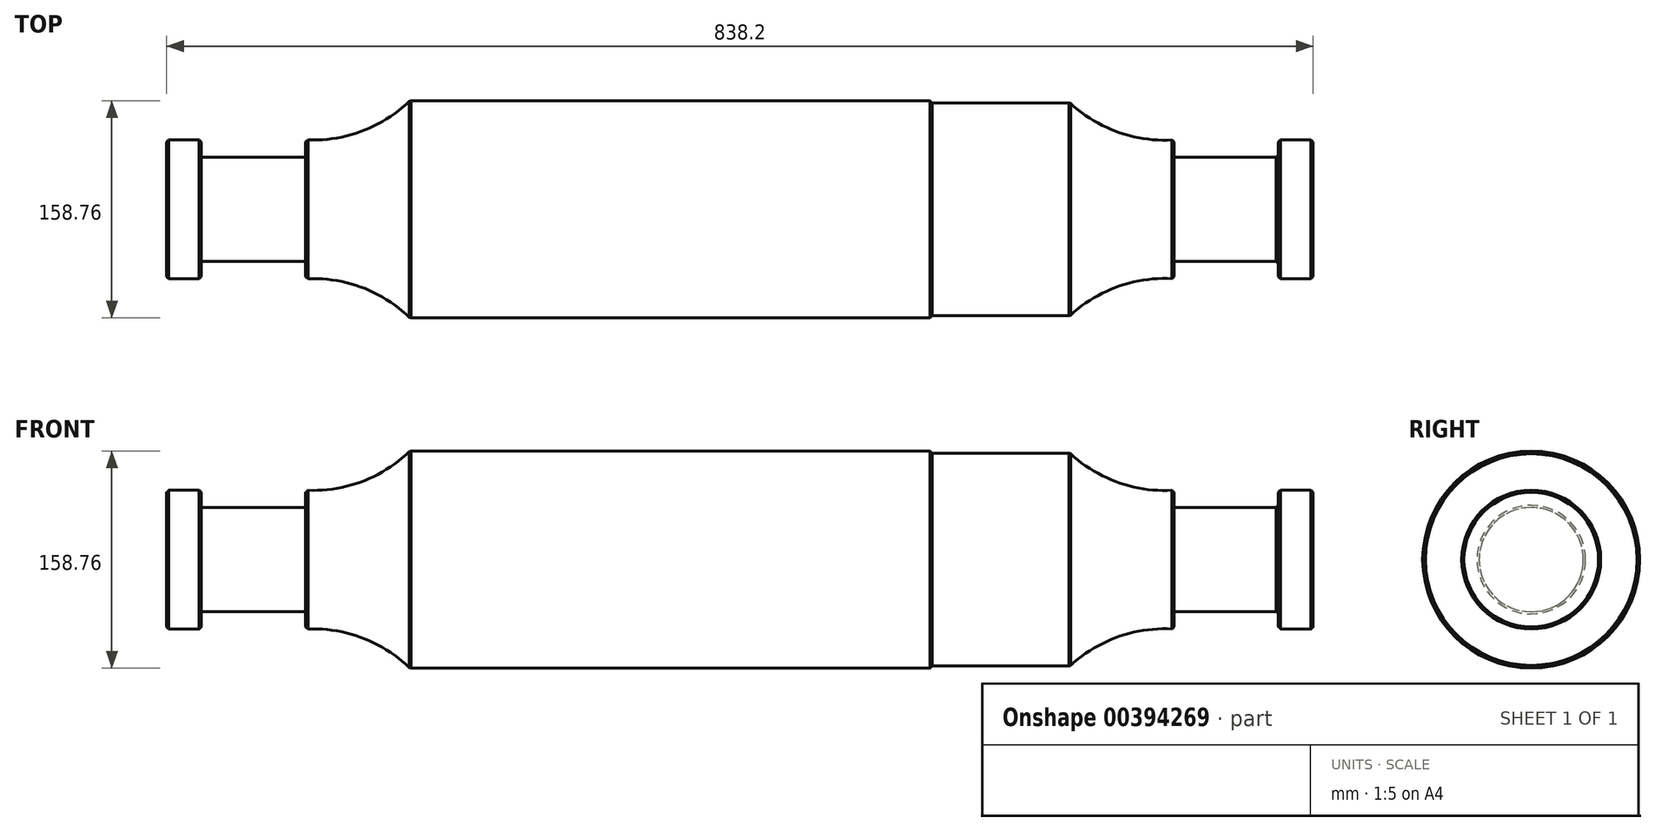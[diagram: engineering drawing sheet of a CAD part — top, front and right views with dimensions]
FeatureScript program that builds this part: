
annotation { "Feature Type Name" : "Feature", "Feature Type Description" : "" }
export const myFeature = defineFeature(function(context is Context, id is Id, definition is map)
    precondition{}
    {
        {
            var Q0;
            Q0=qCreatedBy(makeId("Front.planeOp"),FACE);
            var sketch = newSketch(context, id + "F0", { "sketchPlane" : qUnion([Q0])});
            skLineSegment(sketch, "E0", {"start": v(-447.12, 0) * mm, "end": v(391.08, 0) * mm});
            skLineSegment(sketch, "E1", {"start": v(-447.12, 0) * mm, "end": v(-447.12, 50.8) * mm});
            skLineSegment(sketch, "E2", {"start": v(-447.12, 50.8) * mm, "end": v(-421.72, 50.8) * mm});
            skLineSegment(sketch, "E3", {"start": v(-421.72, 50.8) * mm, "end": v(-421.72, 38.1) * mm});
            skLineSegment(sketch, "E4", {"start": v(-421.72, 38.1) * mm, "end": v(-345.52, 38.1) * mm});
            skLineSegment(sketch, "E5", {"start": v(-345.52, 38.1) * mm, "end": v(-345.52, 50.8) * mm});
            skLineSegment(sketch, "E6", {"start": v(-269.32, 79.37) * mm, "end": v(111.68, 79.38) * mm});
            skLineSegment(sketch, "E7", {"start": v(111.68, 79.38) * mm, "end": v(111.68, 77.79) * mm});
            skLineSegment(sketch, "E8", {"start": v(111.68, 77.79) * mm, "end": v(213.28, 77.79) * mm});
            skLineSegment(sketch, "E9", {"start": v(391.08, 50.8) * mm, "end": v(365.68, 50.8) * mm});
            skLineSegment(sketch, "E10", {"start": v(365.68, 50.8) * mm, "end": v(391.08, 50.8) * mm});
            skLineSegment(sketch, "E11", {"start": v(365.68, 50.8) * mm, "end": v(365.68, 38.1) * mm});
            skLineSegment(sketch, "E12", {"start": v(365.68, 38.1) * mm, "end": v(289.48, 38.1) * mm});
            skLineSegment(sketch, "E13", {"start": v(289.48, 38.1) * mm, "end": v(289.48, 50.8) * mm});
            skArc(sketch, "E14", {"start": v(213.28, 77.79) * mm, "mid": v(248.58, 56.39) * mm, "end": v(289.48, 50.8) * mm});
            skArc(sketch, "E15", {"start": v(-345.52, 50.8) * mm, "mid": v(-304.43, 57.12) * mm, "end": v(-269.32, 79.37) * mm});
            skLineSegment(sketch, "E16", {"start": v(391.08, 50.8) * mm, "end": v(391.08, 0) * mm});
            skSolve(sketch);
        }
        {
            var Q0;
            Q0=makeQuery(id+"F0.imprint","IMPRINT",FACE,{"disambiguationData":[TD([[makeQuery(id+"F0.imprint","IMPRINT",EDGE,{"derivedFrom":sQuery(id+"F0.wireOp",EDGE,"E0")}),1.0]])]});
            var Q1;
            Q1=sQuery(id+"F0.wireOp",EDGE,"E0");
            revolve(context, id + "F1", {"entities" : qUnion([Q0]), "axis" : qUnion([Q1]), "revolveType" : RevolveType.FULL});
        }
        {
            var Q0;
            Q0=makeQuery(id+"F1.opRevolve","SWEPT_EDGE",EDGE,{"disambiguationData":[OSD([sQuery(id+"F0.wireOp",EDGE,"E1"),sQuery(id+"F0.wireOp",EDGE,"E2")])]});
            var Q1;
            Q1=makeQuery(id+"F1.opRevolve","SWEPT_EDGE",EDGE,{"disambiguationData":[OSD([sQuery(id+"F0.wireOp",EDGE,"E2"),sQuery(id+"F0.wireOp",EDGE,"E3")])]});
            var Q2;
            Q2=makeQuery(id+"F1.opRevolve","SWEPT_EDGE",EDGE,{"disambiguationData":[OSD([sQuery(id+"F0.wireOp",EDGE,"E5"),sQuery(id+"F0.wireOp",EDGE,"E15")])]});
            var Q3;
            Q3=makeQuery(id+"F1.opRevolve","SWEPT_EDGE",EDGE,{"disambiguationData":[OSD([sQuery(id+"F0.wireOp",EDGE,"E10"),sQuery(id+"F0.wireOp",EDGE,"E16")])]});
            var Q4;
            Q4=makeQuery(id+"F1.opRevolve","SWEPT_EDGE",EDGE,{"disambiguationData":[OSD([sQuery(id+"F0.wireOp",EDGE,"E10"),sQuery(id+"F0.wireOp",EDGE,"E11")])]});
            var Q5;
            Q5=makeQuery(id+"F1.opRevolve","SWEPT_EDGE",EDGE,{"disambiguationData":[OSD([sQuery(id+"F0.wireOp",EDGE,"E13"),sQuery(id+"F0.wireOp",EDGE,"E14")])]});
            var Q6;
            Q6=makeQuery(id+"F1.opRevolve","SWEPT_EDGE",EDGE,{"disambiguationData":[OSD([sQuery(id+"F0.wireOp",EDGE,"E8"),sQuery(id+"F0.wireOp",EDGE,"E14")])]});
            var Q7;
            Q7=makeQuery(id+"F1.opRevolve","SWEPT_EDGE",EDGE,{"disambiguationData":[OSD([sQuery(id+"F0.wireOp",EDGE,"E6"),sQuery(id+"F0.wireOp",EDGE,"E15")])]});
            chamfer(context, id + "F2", {"entities" : qUnion([Q0, Q1, Q2, Q3, Q4, Q5, Q6, Q7]), "width" : 1.59 * mm, "tangentPropagation" : true});
        }
        {
            var Q0;
            Q0=makeQuery(id+"F1.opRevolve","SWEPT_EDGE",EDGE,{"disambiguationData":[OSD([sQuery(id+"F0.wireOp",EDGE,"E6"),sQuery(id+"F0.wireOp",EDGE,"E7")])]});
            var Q1;
            Q1=makeQuery(id+"F1.opRevolve","SWEPT_FACE",FACE,{"disambiguationData":[OSD([sQuery(id+"F0.wireOp",EDGE,"E8")])]});
            chamfer(context, id + "F3", {"entities" : qUnion([Q0, Q1]), "width" : 0.76 * mm, "tangentPropagation" : true});
        }
    });
